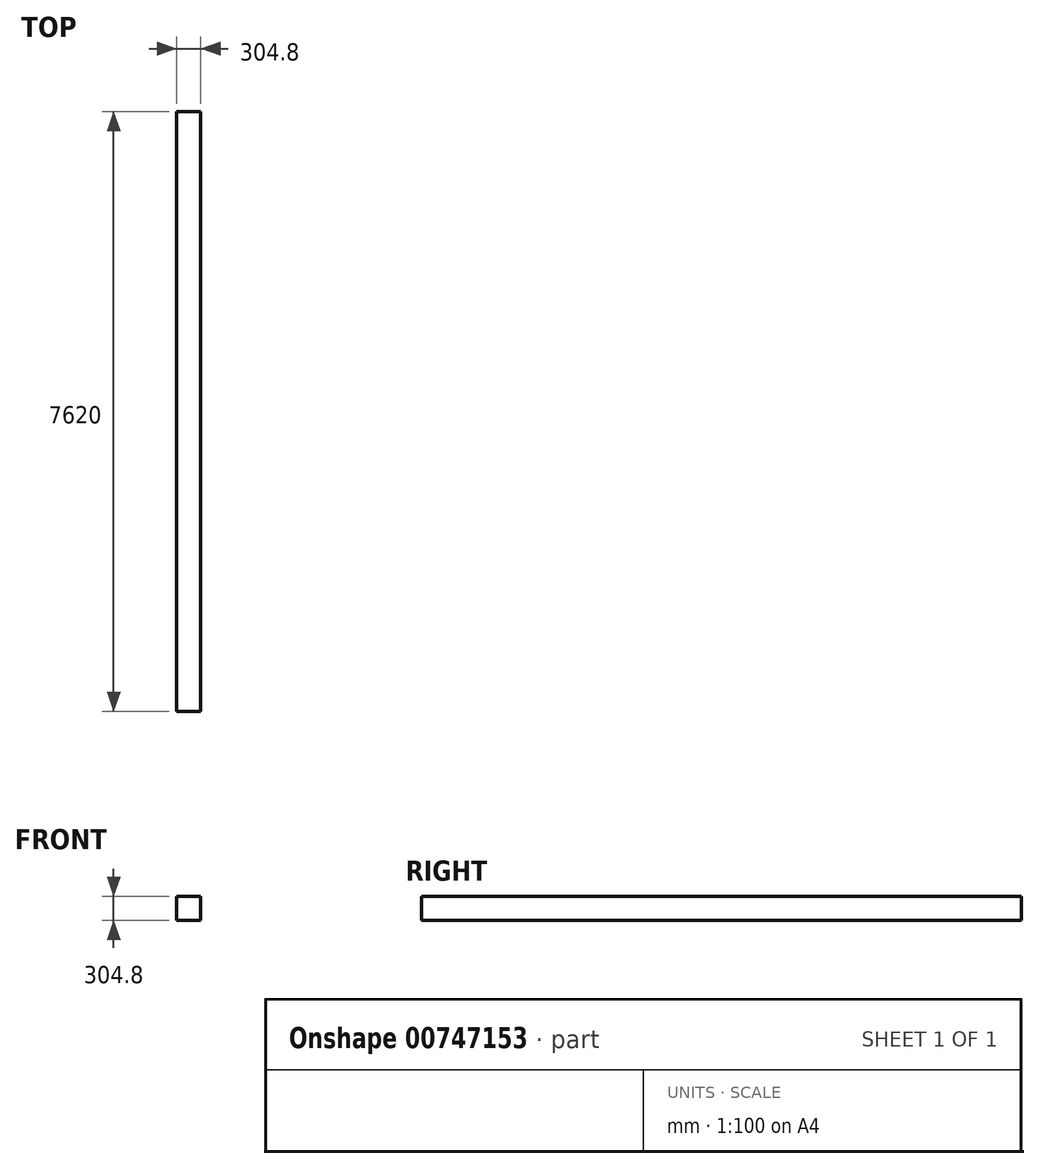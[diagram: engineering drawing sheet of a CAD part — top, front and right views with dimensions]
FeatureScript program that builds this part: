
annotation { "Feature Type Name" : "Feature", "Feature Type Description" : "" }
export const myFeature = defineFeature(function(context is Context, id is Id, definition is map)
    precondition{}
    {
        {
            var Q0;
            Q0=qCreatedBy(makeId("Front.planeOp"),FACE);
            var sketch = newSketch(context, id + "F0", { "sketchPlane" : qUnion([Q0])});
            skLineSegment(sketch, "E0.bottom", {"start": v(-183.9, 162.03) * mm, "end": v(120.9, 162.03) * mm});
            skLineSegment(sketch, "E0.top", {"start": v(-183.9, -142.77) * mm, "end": v(120.9, -142.77) * mm});
            skLineSegment(sketch, "E0.left", {"start": v(-183.9, 162.03) * mm, "end": v(-183.9, -142.77) * mm});
            skLineSegment(sketch, "E0.right", {"start": v(120.9, 162.03) * mm, "end": v(120.9, -142.77) * mm});
            skSolve(sketch);
        }
        {
            var Q0;
            Q0 = qSketchRegion(id + "F0", true);
            extrude(context, id + "F1", {"entities" : qUnion([Q0]), "oppositeDirection" : true, "depth" : 7620 * mm, "offsetDistance" : 25.4 * mm});
        }
    });
